# Revit family: Paper_Towel_Dispenser-Bobrick-Fino-B-9262
name_source: partatom
category: Specialty Equipment
revit_build: Autodesk Revit 2018 (Build: 20170223_1515(x64)
units: mm (PartAtom-declared; Revit-internal decimal feet)

## family parameters
Cut with Voids When Loaded = No
Host = Face
OmniClass Number = 23.40.20.21.14
OmniClass Title = Hand and Hair Dryers
Part Type = Normal
Room Calculation Point = No
Round Connector Dimension = Use Diameter
Shared = Yes

## types (1)
- B-9262
    ADA Compliant = Yes
    Assembly Code = C1030200
    Default Elevation = 0"
    Description = Fino Collection Surface Mounted Paper Towel Dispenser
    Finish = Stainless_Steel-Bobrick-Type_304-Satin_Finish
    Height = 13 5/8"
    Installation Type = Wall Mounted
    Length = 11 11/16"
    Manufacturer = Bobrick
    Material = Stainless_Steel-Bobrick-Type_304-Satin_Finish
    Model = B-9262
    Mounting Height From Floor = 30"
    Price = Prices may vary. Please consult Manufacturer Representative for most up-to-date price list.
    URL = https://www.bobrick.com
    Width = 3 15/16"

## geometry (parser evidence)
native form markers: Sweep x3
no freeform markers — native parametric forms only
